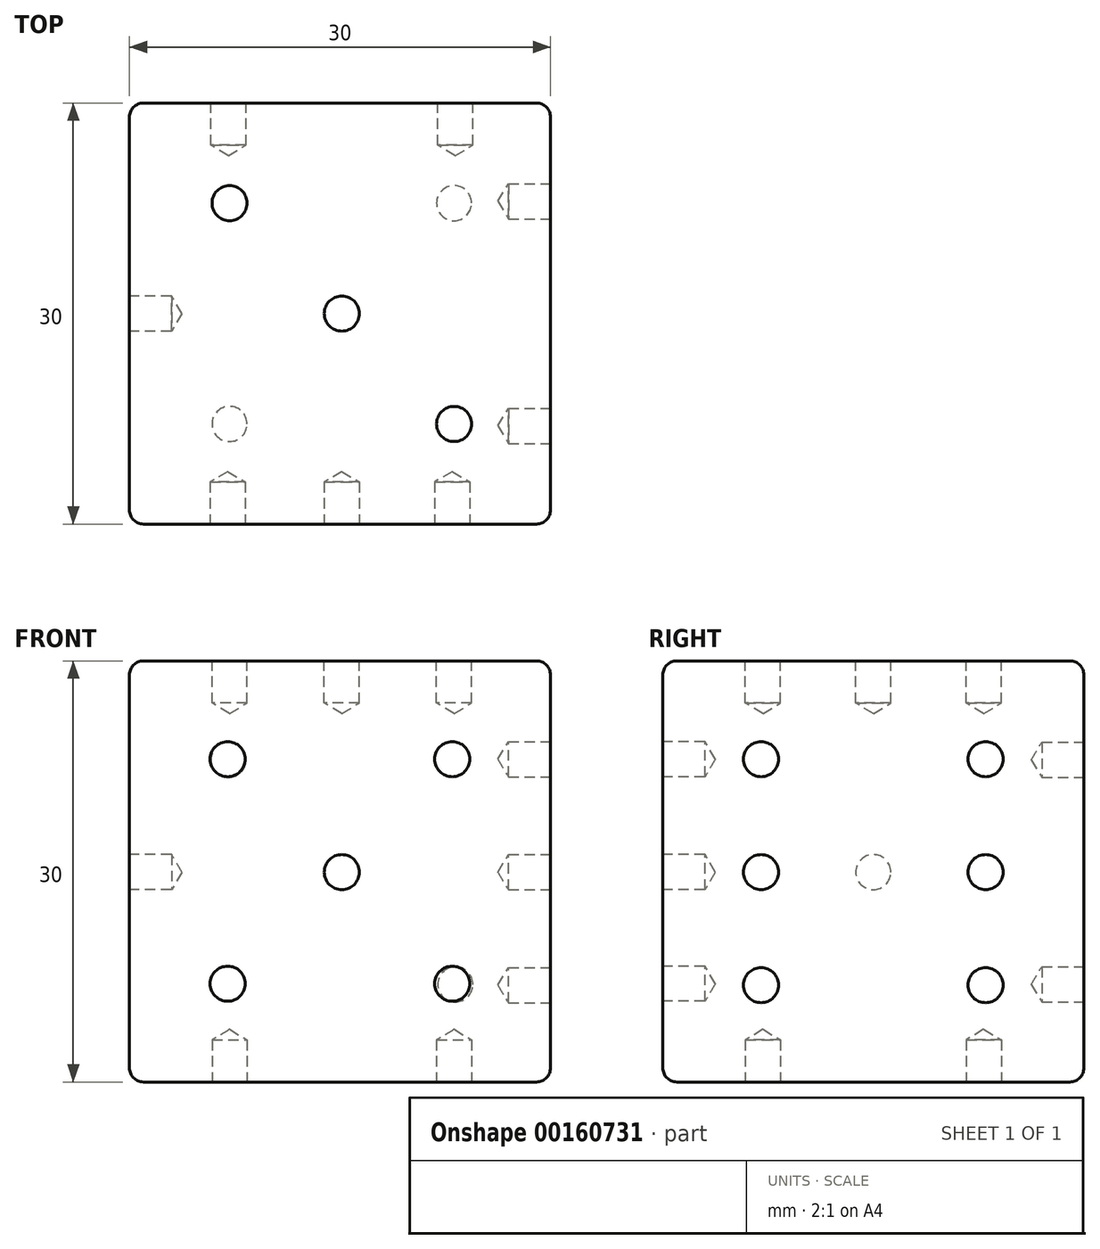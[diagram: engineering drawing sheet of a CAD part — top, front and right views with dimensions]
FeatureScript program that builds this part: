
annotation { "Feature Type Name" : "Feature", "Feature Type Description" : "" }
export const myFeature = defineFeature(function(context is Context, id is Id, definition is map)
    precondition{}
    {
        {
            var Q0;
            Q0=qCreatedBy(makeId("Front.planeOp"),FACE);
            var sketch = newSketch(context, id + "F0", { "sketchPlane" : qUnion([Q0])});
            skLineSegment(sketch, "E0", {"start": v(-15.13, 15.05) * mm, "end": v(14.87, 15.05) * mm});
            skLineSegment(sketch, "E1", {"start": v(14.87, 15.05) * mm, "end": v(14.87, -14.95) * mm});
            skLineSegment(sketch, "E2", {"start": v(14.87, -14.95) * mm, "end": v(-15.13, -14.95) * mm});
            skLineSegment(sketch, "E3", {"start": v(-15.13, -14.95) * mm, "end": v(-15.13, 15.05) * mm});
            skLineSegment(sketch, "E4", {"start": v(14.87, 15.05) * mm, "end": v(-15.13, -14.95) * mm});
            skLineSegment(sketch, "E5", {"start": v(-15.13, 15.05) * mm, "end": v(14.87, -14.95) * mm});
            skSolve(sketch);
        }
        {
            var Q0;
            Q0 = qSketchRegion(id + "F0", true);
            extrude(context, id + "F1", {"entities" : qUnion([Q0]), "endBound" : BoundingType.SYMMETRIC, "depth" : 30 * mm});
        }
        {
            var Q0;
            Q0=makeQuery(id+"F1.opExtrude","CAP_EDGE",EDGE,{"disambiguationData":[OSD([sQuery(id+"F0.wireOp",EDGE,"E0")])],"isStart":false});
            var Q1;
            Q1=makeQuery(id+"F1.opExtrude","SWEPT_EDGE",EDGE,{"disambiguationData":[OSD([sQuery(id+"F0.wireOp",EDGE,"E0"),sQuery(id+"F0.wireOp",EDGE,"E1")])]});
            var Q2;
            Q2=makeQuery(id+"F1.opExtrude","CAP_EDGE",EDGE,{"disambiguationData":[OSD([sQuery(id+"F0.wireOp",EDGE,"E0")])],"isStart":true});
            var Q3;
            Q3=makeQuery(id+"F1.opExtrude","SWEPT_EDGE",EDGE,{"disambiguationData":[OSD([sQuery(id+"F0.wireOp",EDGE,"E0"),sQuery(id+"F0.wireOp",EDGE,"E3")])]});
            var Q4;
            Q4=makeQuery(id+"F1.opExtrude","CAP_EDGE",EDGE,{"disambiguationData":[OSD([sQuery(id+"F0.wireOp",EDGE,"E3")])],"isStart":true});
            var Q5;
            Q5=makeQuery(id+"F1.opExtrude","CAP_EDGE",EDGE,{"disambiguationData":[OSD([sQuery(id+"F0.wireOp",EDGE,"E1")])],"isStart":true});
            var Q6;
            Q6=makeQuery(id+"F1.opExtrude","CAP_EDGE",EDGE,{"disambiguationData":[OSD([sQuery(id+"F0.wireOp",EDGE,"E1")])],"isStart":false});
            var Q7;
            Q7=makeQuery(id+"F1.opExtrude","CAP_EDGE",EDGE,{"disambiguationData":[OSD([sQuery(id+"F0.wireOp",EDGE,"E2")])],"isStart":false});
            var Q8;
            Q8=makeQuery(id+"F1.opExtrude","SWEPT_EDGE",EDGE,{"disambiguationData":[OSD([sQuery(id+"F0.wireOp",EDGE,"E1"),sQuery(id+"F0.wireOp",EDGE,"E2")])]});
            var Q9;
            Q9=makeQuery(id+"F1.opExtrude","SWEPT_EDGE",EDGE,{"disambiguationData":[OSD([sQuery(id+"F0.wireOp",EDGE,"E2"),sQuery(id+"F0.wireOp",EDGE,"E3")])]});
            var Q10;
            Q10=makeQuery(id+"F1.opExtrude","CAP_EDGE",EDGE,{"disambiguationData":[OSD([sQuery(id+"F0.wireOp",EDGE,"E2")])],"isStart":true});
            fillet(context, id + "F2", {"entities" : qUnion([Q0, Q1, Q2, Q3, Q4, Q5, Q6, Q7, Q8, Q9, Q10]), "radius" : 1 * mm, "tangentPropagation" : true, "allowEdgeOverflow" : false});
        }
        {
            var Q0;
            Q0=makeQuery(id+"F1.opExtrude","CAP_EDGE",EDGE,{"disambiguationData":[OSD([sQuery(id+"F0.wireOp",EDGE,"E3")])],"isStart":false});
            fillet(context, id + "F3", {"entities" : qUnion([Q0]), "radius" : 1 * mm, "tangentPropagation" : true, "allowEdgeOverflow" : false});
        }
        {
            var Q0;
            Q0=makeQuery(id+"F1.opExtrude","CAP_FACE",FACE,{"disambiguationData":[OSD([sQuery(id+"F0.wireOp",EDGE,"E0"),sQuery(id+"F0.wireOp",EDGE,"E1"),sQuery(id+"F0.wireOp",EDGE,"E2"),sQuery(id+"F0.wireOp",EDGE,"E3")])],"isStart":false});
            var sketch = newSketch(context, id + "F4", { "sketchPlane" : qUnion([Q0])});
            skLineSegment(sketch, "E6", {"start": v(-14.13, 14.05) * mm, "end": v(13.87, -13.95) * mm});
            skLineSegment(sketch, "E7", {"start": v(13.87, 14.05) * mm, "end": v(-14.13, -13.95) * mm});
            skLineSegment(sketch, "E8.bottom", {"start": v(-8.13, 8.05) * mm, "end": v(7.87, 8.05) * mm});
            skLineSegment(sketch, "E8.top", {"start": v(-8.13, -7.95) * mm, "end": v(7.87, -7.95) * mm});
            skLineSegment(sketch, "E8.left", {"start": v(-8.13, 8.05) * mm, "end": v(-8.13, -7.95) * mm});
            skLineSegment(sketch, "E8.right", {"start": v(7.87, 8.05) * mm, "end": v(7.87, -7.95) * mm});
            skPoint(sketch, "E8.middle", {"position": v(-0.13, 0.05) * mm});
            skPoint(sketch, "E9", {"position": v(-8.13, 8.05) * mm});
            skPoint(sketch, "E10", {"position": v(-8.13, -7.95) * mm});
            skPoint(sketch, "E11", {"position": v(7.87, -7.95) * mm});
            skPoint(sketch, "E12", {"position": v(7.87, 8.05) * mm});
            skPoint(sketch, "E13", {"position": v(0, 0) * mm});
            skSolve(sketch);
        }
        {
            var Q0;
            Q0=makeQuery(id+"F1.opExtrude","SWEPT_FACE",FACE,{"disambiguationData":[OSD([sQuery(id+"F0.wireOp",EDGE,"E3")])]});
            var sketch = newSketch(context, id + "F5", { "sketchPlane" : qUnion([Q0])});
            skLineSegment(sketch, "E14", {"start": v(-14, 14.05) * mm, "end": v(14, -13.95) * mm});
            skLineSegment(sketch, "E15", {"start": v(14, 14.05) * mm, "end": v(-14, -13.95) * mm});
            skPoint(sketch, "E16", {"position": v(0, 0) * mm});
            skLineSegment(sketch, "E17.bottom", {"start": v(0.9, 0.95) * mm, "end": v(-0.9, 0.95) * mm});
            skLineSegment(sketch, "E17.top", {"start": v(0.9, -0.95) * mm, "end": v(-0.9, -0.95) * mm});
            skLineSegment(sketch, "E17.left", {"start": v(0.9, 0.95) * mm, "end": v(0.9, -0.95) * mm});
            skLineSegment(sketch, "E17.right", {"start": v(-0.9, 0.95) * mm, "end": v(-0.9, -0.95) * mm});
            skSolve(sketch);
        }
        {
            var Q0;
            Q0=makeQuery(id+"F1.opExtrude","SWEPT_FACE",FACE,{"disambiguationData":[OSD([sQuery(id+"F0.wireOp",EDGE,"E1")])]});
            var sketch = newSketch(context, id + "F6", { "sketchPlane" : qUnion([Q0])});
            skLineSegment(sketch, "E18", {"start": v(-14, 14.05) * mm, "end": v(14, -13.95) * mm});
            skLineSegment(sketch, "E19", {"start": v(14, 14.05) * mm, "end": v(-14, -13.95) * mm});
            skLineSegment(sketch, "E20.bottom", {"start": v(8, 8.05) * mm, "end": v(-8, 8.05) * mm});
            skLineSegment(sketch, "E20.top", {"start": v(8, -8.05) * mm, "end": v(-8, -8.05) * mm});
            skLineSegment(sketch, "E20.left", {"start": v(8, 8.05) * mm, "end": v(8, -8.05) * mm});
            skLineSegment(sketch, "E20.right", {"start": v(-8, 8.05) * mm, "end": v(-8, -8.05) * mm});
            skPoint(sketch, "E20.middle", {"position": v(0, 0) * mm});
            skPoint(sketch, "E21", {"position": v(-8, 8.05) * mm});
            skPoint(sketch, "E22", {"position": v(-8, 0) * mm});
            skPoint(sketch, "E23", {"position": v(-8, -8.05) * mm});
            skPoint(sketch, "E24", {"position": v(8, -8.05) * mm});
            skPoint(sketch, "E25", {"position": v(8, 0) * mm});
            skPoint(sketch, "E26", {"position": v(8, 8.05) * mm});
            skSolve(sketch);
        }
        {
            var Q0;
            Q0=makeQuery(id+"F1.opExtrude","CAP_FACE",FACE,{"disambiguationData":[OSD([sQuery(id+"F0.wireOp",EDGE,"E0"),sQuery(id+"F0.wireOp",EDGE,"E1"),sQuery(id+"F0.wireOp",EDGE,"E2"),sQuery(id+"F0.wireOp",EDGE,"E3")])],"isStart":true});
            var sketch = newSketch(context, id + "F7", { "sketchPlane" : qUnion([Q0])});
            skLineSegment(sketch, "E27", {"start": v(-13.87, 14.05) * mm, "end": v(14.13, -13.95) * mm});
            skLineSegment(sketch, "E28", {"start": v(14.13, 14.05) * mm, "end": v(-13.87, -13.95) * mm});
            skLineSegment(sketch, "E29.bottom", {"start": v(8.08, 8) * mm, "end": v(-8.08, 8) * mm});
            skLineSegment(sketch, "E29.top", {"start": v(8.08, -8) * mm, "end": v(-8.08, -8) * mm});
            skLineSegment(sketch, "E29.left", {"start": v(8.08, 8) * mm, "end": v(8.08, -8) * mm});
            skLineSegment(sketch, "E29.right", {"start": v(-8.08, 8) * mm, "end": v(-8.08, -8) * mm});
            skPoint(sketch, "E29.middle", {"position": v(0, 0) * mm});
            skPoint(sketch, "E30", {"position": v(8.08, 8) * mm});
            skPoint(sketch, "E31", {"position": v(-8.08, -8) * mm});
            skSolve(sketch);
        }
        {
            var Q0;
            Q0=makeQuery(id+"F1.opExtrude","SWEPT_FACE",FACE,{"disambiguationData":[OSD([sQuery(id+"F0.wireOp",EDGE,"E2")])]});
            var sketch = newSketch(context, id + "F8", { "sketchPlane" : qUnion([Q0])});
            skLineSegment(sketch, "E32", {"start": v(-13.24, 13.1) * mm, "end": v(13.87, -14) * mm});
            skLineSegment(sketch, "E33", {"start": v(13.87, 14) * mm, "end": v(-14.13, -14) * mm});
            skLineSegment(sketch, "E34", {"start": v(13.87, -14) * mm, "end": v(-13.24, 13.1) * mm});
            skLineSegment(sketch, "E35", {"start": v(-14.13, -14) * mm, "end": v(13.87, 14) * mm});
            skLineSegment(sketch, "E36.bottom", {"start": v(-8, -7.87) * mm, "end": v(8, -7.87) * mm});
            skLineSegment(sketch, "E36.top", {"start": v(-8, 7.87) * mm, "end": v(8, 7.87) * mm});
            skLineSegment(sketch, "E36.left", {"start": v(-8, -7.87) * mm, "end": v(-8, 7.87) * mm});
            skLineSegment(sketch, "E36.right", {"start": v(8, -7.87) * mm, "end": v(8, 7.87) * mm});
            skPoint(sketch, "E36.middle", {"position": v(0, 0) * mm});
            skPoint(sketch, "E37", {"position": v(-8, -7.87) * mm});
            skPoint(sketch, "E38", {"position": v(8, -7.87) * mm});
            skPoint(sketch, "E39", {"position": v(8, 7.87) * mm});
            skPoint(sketch, "E40", {"position": v(-8, 7.87) * mm});
            skSolve(sketch);
        }
        {
            var Q0;
            Q0=makeQuery(id+"F1.opExtrude","SWEPT_FACE",FACE,{"disambiguationData":[OSD([sQuery(id+"F0.wireOp",EDGE,"E0")])]});
            var sketch = newSketch(context, id + "F9", { "sketchPlane" : qUnion([Q0])});
            skLineSegment(sketch, "E41", {"start": v(-13.24, -13.1) * mm, "end": v(13.87, 14) * mm});
            skLineSegment(sketch, "E42", {"start": v(-14.13, 14) * mm, "end": v(13.87, -14) * mm});
            skLineSegment(sketch, "E43.bottom", {"start": v(-8, -7.87) * mm, "end": v(8, -7.87) * mm});
            skLineSegment(sketch, "E43.top", {"start": v(-8, 7.87) * mm, "end": v(8, 7.87) * mm});
            skLineSegment(sketch, "E43.left", {"start": v(-8, -7.87) * mm, "end": v(-8, 7.87) * mm});
            skLineSegment(sketch, "E43.right", {"start": v(8, -7.87) * mm, "end": v(8, 7.87) * mm});
            skPoint(sketch, "E43.middle", {"position": v(0, 0) * mm});
            skPoint(sketch, "E44", {"position": v(-8, 7.87) * mm});
            skPoint(sketch, "E45", {"position": v(8, -7.87) * mm});
            skSolve(sketch);
        }
        {
            var Q0;
            Q0=sQuery(id+"F5.wireOp",VERTEX,"E16");
            var Q1;
            Q1=makeQuery(id+"F1.opExtrude","SWEPT_BODY",BODY,{"disambiguationData":[OSD([sQuery(id+"F0.wireOp",EDGE,"E0"),sQuery(id+"F0.wireOp",EDGE,"E1"),sQuery(id+"F0.wireOp",EDGE,"E2"),sQuery(id+"F0.wireOp",EDGE,"E3")])]});
            hole(context, id + "F10", {"style" : HoleStyle.SIMPLE, "endStyle" : HoleEndStyle.BLIND, "holeDiameter" : 2.5 * mm, "holeDepth" : 3 * mm, "locations" : qUnion([Q0]), "scope" : qUnion([Q1])});
        }
        {
            var Q0;
            Q0=sQuery(id+"F7.wireOp",VERTEX,"E30");
            var Q1;
            Q1=sQuery(id+"F7.wireOp",VERTEX,"E31");
            var Q2;
            Q2=makeQuery(id+"F1.opExtrude","SWEPT_BODY",BODY,{"disambiguationData":[OSD([sQuery(id+"F0.wireOp",EDGE,"E0"),sQuery(id+"F0.wireOp",EDGE,"E1"),sQuery(id+"F0.wireOp",EDGE,"E2"),sQuery(id+"F0.wireOp",EDGE,"E3")])]});
            hole(context, id + "F11", {"style" : HoleStyle.SIMPLE, "endStyle" : HoleEndStyle.BLIND, "holeDiameter" : 2.5 * mm, "holeDepth" : 3 * mm, "locations" : qUnion([Q0, Q1]), "scope" : qUnion([Q2])});
        }
        {
            var Q0;
            Q0=sQuery(id+"F9.wireOp",VERTEX,"E44");
            var Q1;
            Q1=sQuery(id+"F9.wireOp",VERTEX,"E43.middle");
            var Q2;
            Q2=sQuery(id+"F9.wireOp",VERTEX,"E45");
            var Q3;
            Q3=makeQuery(id+"F1.opExtrude","SWEPT_BODY",BODY,{"disambiguationData":[OSD([sQuery(id+"F0.wireOp",EDGE,"E0"),sQuery(id+"F0.wireOp",EDGE,"E1"),sQuery(id+"F0.wireOp",EDGE,"E2"),sQuery(id+"F0.wireOp",EDGE,"E3")])]});
            hole(context, id + "F12", {"style" : HoleStyle.SIMPLE, "endStyle" : HoleEndStyle.BLIND, "holeDiameter" : 2.5 * mm, "holeDepth" : 3 * mm, "locations" : qUnion([Q0, Q1, Q2]), "scope" : qUnion([Q3])});
        }
        {
            var Q0;
            Q0=sQuery(id+"F8.wireOp",VERTEX,"E40");
            var Q1;
            Q1=sQuery(id+"F8.wireOp",VERTEX,"E39");
            var Q2;
            Q2=sQuery(id+"F8.wireOp",VERTEX,"E38");
            var Q3;
            Q3=sQuery(id+"F8.wireOp",VERTEX,"E37");
            var Q4;
            Q4=makeQuery(id+"F1.opExtrude","SWEPT_BODY",BODY,{"disambiguationData":[OSD([sQuery(id+"F0.wireOp",EDGE,"E0"),sQuery(id+"F0.wireOp",EDGE,"E1"),sQuery(id+"F0.wireOp",EDGE,"E2"),sQuery(id+"F0.wireOp",EDGE,"E3")])]});
            hole(context, id + "F13", {"style" : HoleStyle.SIMPLE, "endStyle" : HoleEndStyle.BLIND, "holeDiameter" : 2.5 * mm, "holeDepth" : 3 * mm, "locations" : qUnion([Q0, Q1, Q2, Q3]), "scope" : qUnion([Q4])});
        }
        {
            var Q0;
            Q0=sQuery(id+"F6.wireOp",VERTEX,"E21");
            var Q1;
            Q1=sQuery(id+"F6.wireOp",VERTEX,"E22");
            var Q2;
            Q2=sQuery(id+"F6.wireOp",VERTEX,"E23");
            var Q3;
            Q3=sQuery(id+"F6.wireOp",VERTEX,"E24");
            var Q4;
            Q4=sQuery(id+"F6.wireOp",VERTEX,"E25");
            var Q5;
            Q5=sQuery(id+"F6.wireOp",VERTEX,"E26");
            var Q6;
            Q6=makeQuery(id+"F1.opExtrude","SWEPT_BODY",BODY,{"disambiguationData":[OSD([sQuery(id+"F0.wireOp",EDGE,"E0"),sQuery(id+"F0.wireOp",EDGE,"E1"),sQuery(id+"F0.wireOp",EDGE,"E2"),sQuery(id+"F0.wireOp",EDGE,"E3")])]});
            hole(context, id + "F14", {"style" : HoleStyle.SIMPLE, "endStyle" : HoleEndStyle.BLIND, "holeDiameter" : 2.5 * mm, "holeDepth" : 3 * mm, "locations" : qUnion([Q0, Q1, Q2, Q3, Q4, Q5]), "scope" : qUnion([Q6])});
        }
        {
            var Q0;
            Q0=sQuery(id+"F4.wireOp",VERTEX,"E9");
            var Q1;
            Q1=sQuery(id+"F4.wireOp",VERTEX,"E13");
            var Q2;
            Q2=sQuery(id+"F4.wireOp",VERTEX,"E12");
            var Q3;
            Q3=sQuery(id+"F4.wireOp",VERTEX,"E11");
            var Q4;
            Q4=sQuery(id+"F4.wireOp",VERTEX,"E10");
            var Q5;
            Q5=makeQuery(id+"F1.opExtrude","SWEPT_BODY",BODY,{"disambiguationData":[OSD([sQuery(id+"F0.wireOp",EDGE,"E0"),sQuery(id+"F0.wireOp",EDGE,"E1"),sQuery(id+"F0.wireOp",EDGE,"E2"),sQuery(id+"F0.wireOp",EDGE,"E3")])]});
            hole(context, id + "F15", {"style" : HoleStyle.SIMPLE, "endStyle" : HoleEndStyle.BLIND, "holeDiameter" : 2.5 * mm, "holeDepth" : 3 * mm, "locations" : qUnion([Q0, Q1, Q2, Q3, Q4]), "scope" : qUnion([Q5])});
        }
    });
